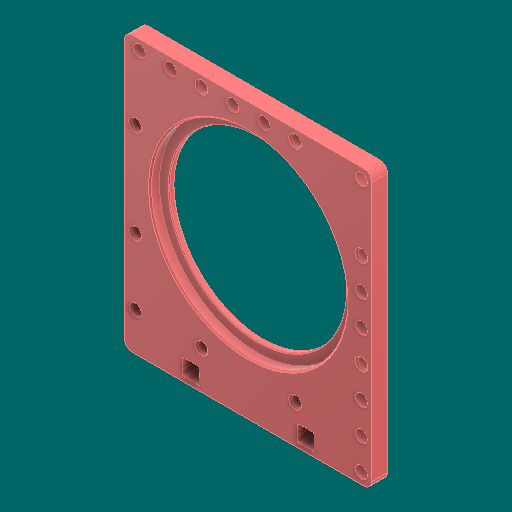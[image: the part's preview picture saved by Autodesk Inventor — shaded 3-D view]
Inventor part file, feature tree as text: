
AUTODESK INVENTOR PART (.ipt)
format: ipt  version: 2023.1 (Build 271208000, 208)  size: 614,400 bytes
history: native  units: in
note: dims shown in document units (in); Inventor stores cm internally (conversion verified against a paired STEP export)
features: chamfer x4, sketch x2, revolve x1, extrude x1, fillet x1
ambient origin geometry x8: Origin, YZ Plane, XZ Plane, XY Plane, X Axis, Y Axis, Z Axis, Center Point
bodies: Solid1 (feature_tree)
feature tree (9):
  revolve  "Revolution1"  [1 undecoded]
  extrude  "Extrusion1"  TaperAngle=360.0deg  [1 undecoded]
  chamfer  "Chamfer1"  Distance=0.1562in
  chamfer  "Chamfer2"  Distance=0.3397in
  chamfer  "Chamfer3"  Distance=3.0in
  chamfer  "Chamfer4"  Distance=1.2in
  fillet  "Fillet1"  Radius=0.26in
  sketch  "Sketch1"  dims[d2=3.1437in d5=0.25in]
  sketch  "Sketch2"  dims[d7=0.2in d8=360.0deg d9=0.1562in d10=0.3397in d16=3.0in d17=1.2in d18=0.26in d19=0.26in d20=0.26in d21=0.26in d24=22.5deg d25=3.1496in d27=360.0deg d29=1.3386in d30=2.2835in d31=1.0in d32=0.27in d35=1.5in d36=0.19in d37=0.5in d38=0.19in d39=1.1811in d41=0.5in d42=0.3937in d44=1.0in d48=0.5in d49=0.19in d50=0.5in d51=0.5in d52=0.7874in d54=0.5in d55=0.3937in d57=1.0in d59=0.25in d60=0.0in d61=0.0236in d62=0.125in d63=45.0deg d64=0.7874in d66=90.0deg d68=0.0236in d69=0.125in d70=45.0deg d71=0.19in d72=3.6in d73=0.33in d74=0.1in d76=0.0118in d77=0.125in d78=45.0deg d79=2.8346in d80=0.0236in d81=0.125in d82=45.0deg d83=0.125in]
note: 2 required parameter values undecoded (feature->parameter linkage not recoverable at this tier; creation-order binding heuristic only, values carry confidence <= 0.55)